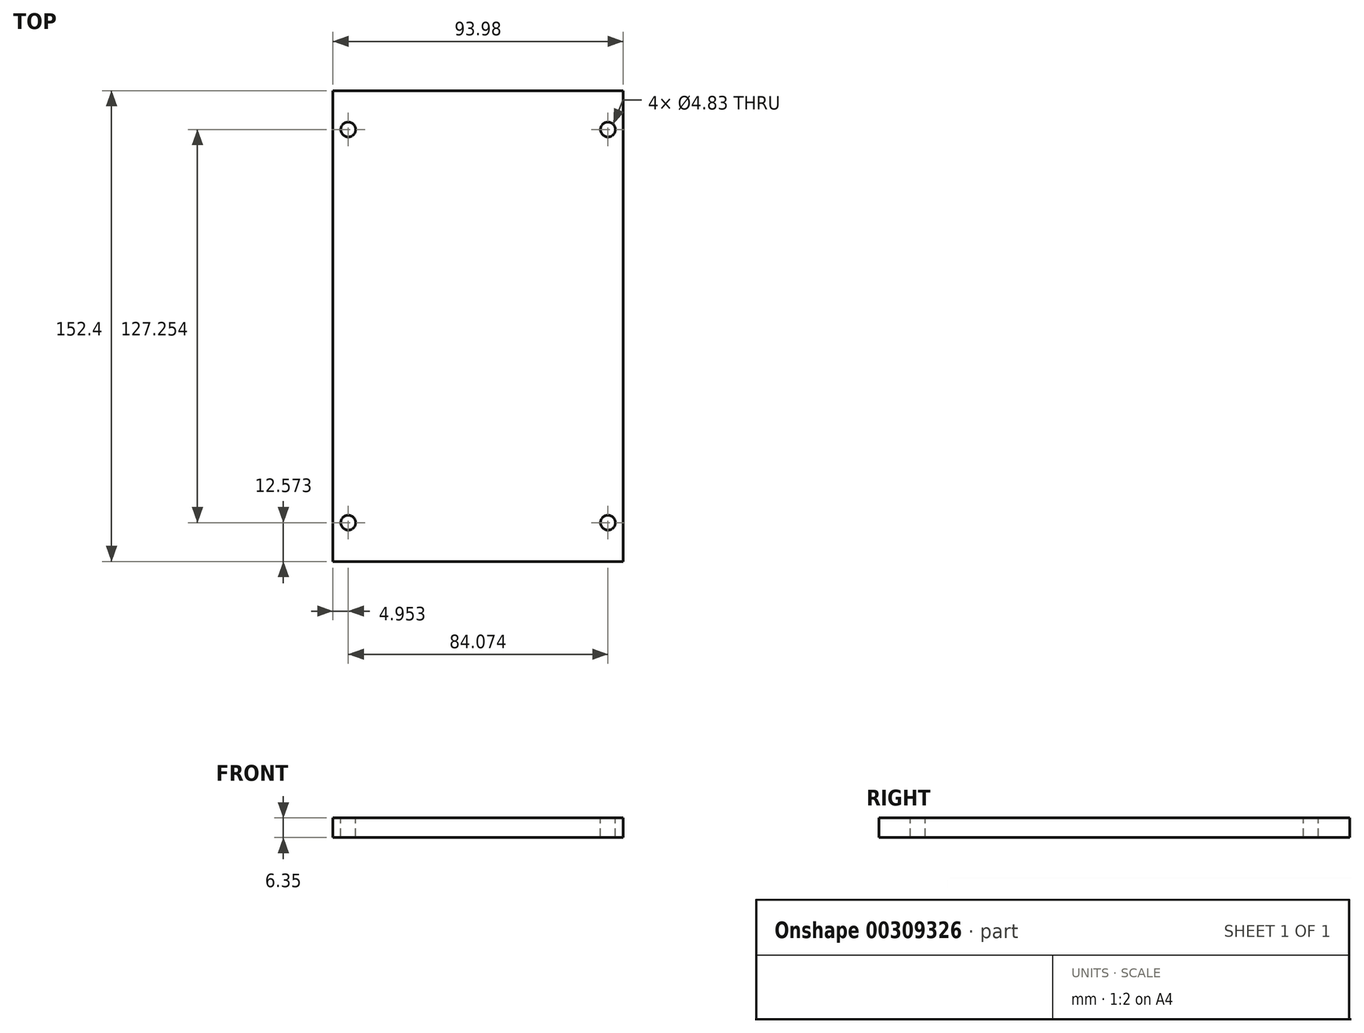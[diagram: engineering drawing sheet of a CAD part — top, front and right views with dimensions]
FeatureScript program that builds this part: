
annotation { "Feature Type Name" : "Feature", "Feature Type Description" : "" }
export const myFeature = defineFeature(function(context is Context, id is Id, definition is map)
    precondition{}
    {
        {
            var Q0;
            Q0=qCreatedBy(makeId("Front.planeOp"),FACE);
            var sketch = newSketch(context, id + "F0", { "sketchPlane" : qUnion([Q0])});
            skLineSegment(sketch, "E0.bottom", {"start": v(0, 0) * mm, "end": v(93.98, 0) * mm});
            skLineSegment(sketch, "E0.top", {"start": v(0, 6.35) * mm, "end": v(93.98, 6.35) * mm});
            skLineSegment(sketch, "E0.left", {"start": v(0, 0) * mm, "end": v(0, 6.35) * mm});
            skLineSegment(sketch, "E0.right", {"start": v(93.98, 0) * mm, "end": v(93.98, 6.35) * mm});
            skSolve(sketch);
        }
        {
            var Q0;
            Q0=makeQuery(id+"F0.imprint","IMPRINT",FACE,{"disambiguationData":[TD([[makeQuery(id+"F0.imprint","IMPRINT",EDGE,{"derivedFrom":sQuery(id+"F0.wireOp",EDGE,"E0.bottom")}),1.0]])]});
            extrude(context, id + "F1", {"entities" : qUnion([Q0]), "depth" : 152.4 * mm});
        }
        {
            var Q0;
            Q0=makeQuery(id+"F1.opExtrude","SWEPT_FACE",FACE,{"disambiguationData":[OSD([sQuery(id+"F0.wireOp",EDGE,"E0.top")])]});
            var sketch = newSketch(context, id + "F2", { "sketchPlane" : qUnion([Q0])});
            skCircle(sketch, "E1", {"center": v(4.95, -12.57) * mm, "radius": 2.41 * mm});
            skCircle(sketch, "E2", {"center": v(-180.25, 190.15) * mm, "radius": 3.24 * mm});
            skCircle(sketch, "E3", {"center": v(89.03, -12.57) * mm, "radius": 2.41 * mm});
            skCircle(sketch, "E4", {"center": v(4.95, -139.83) * mm, "radius": 2.41 * mm});
            skCircle(sketch, "E5", {"center": v(89.03, -139.83) * mm, "radius": 2.41 * mm});
            skSolve(sketch);
        }
        {
            var Q0;
            Q0=makeQuery(id+"F2.imprint","IMPRINT",FACE,{"disambiguationData":[TD([[makeQuery(id+"F2.imprint","IMPRINT",EDGE,{"derivedFrom":sQuery(id+"F2.wireOp",EDGE,"E3")}),1.0]])]});
            var Q1;
            Q1=makeQuery(id+"F2.imprint","IMPRINT",FACE,{"disambiguationData":[TD([[makeQuery(id+"F2.imprint","IMPRINT",EDGE,{"derivedFrom":sQuery(id+"F2.wireOp",EDGE,"E1")}),1.0]])]});
            var Q2;
            Q2=makeQuery(id+"F2.imprint","IMPRINT",FACE,{"disambiguationData":[TD([[makeQuery(id+"F2.imprint","IMPRINT",EDGE,{"derivedFrom":sQuery(id+"F2.wireOp",EDGE,"E5")}),1.0]])]});
            var Q3;
            Q3=makeQuery(id+"F2.imprint","IMPRINT",FACE,{"disambiguationData":[TD([[makeQuery(id+"F2.imprint","IMPRINT",EDGE,{"derivedFrom":sQuery(id+"F2.wireOp",EDGE,"E4")}),1.0]])]});
            extrude(context, id + "F3", {"entities" : qUnion([Q0, Q1, Q2, Q3]), "operationType" : NewBodyOperationType.REMOVE, "endBound" : BoundingType.THROUGH_ALL, "oppositeDirection" : true, "depth" : 25.4 * mm});
        }
    });
